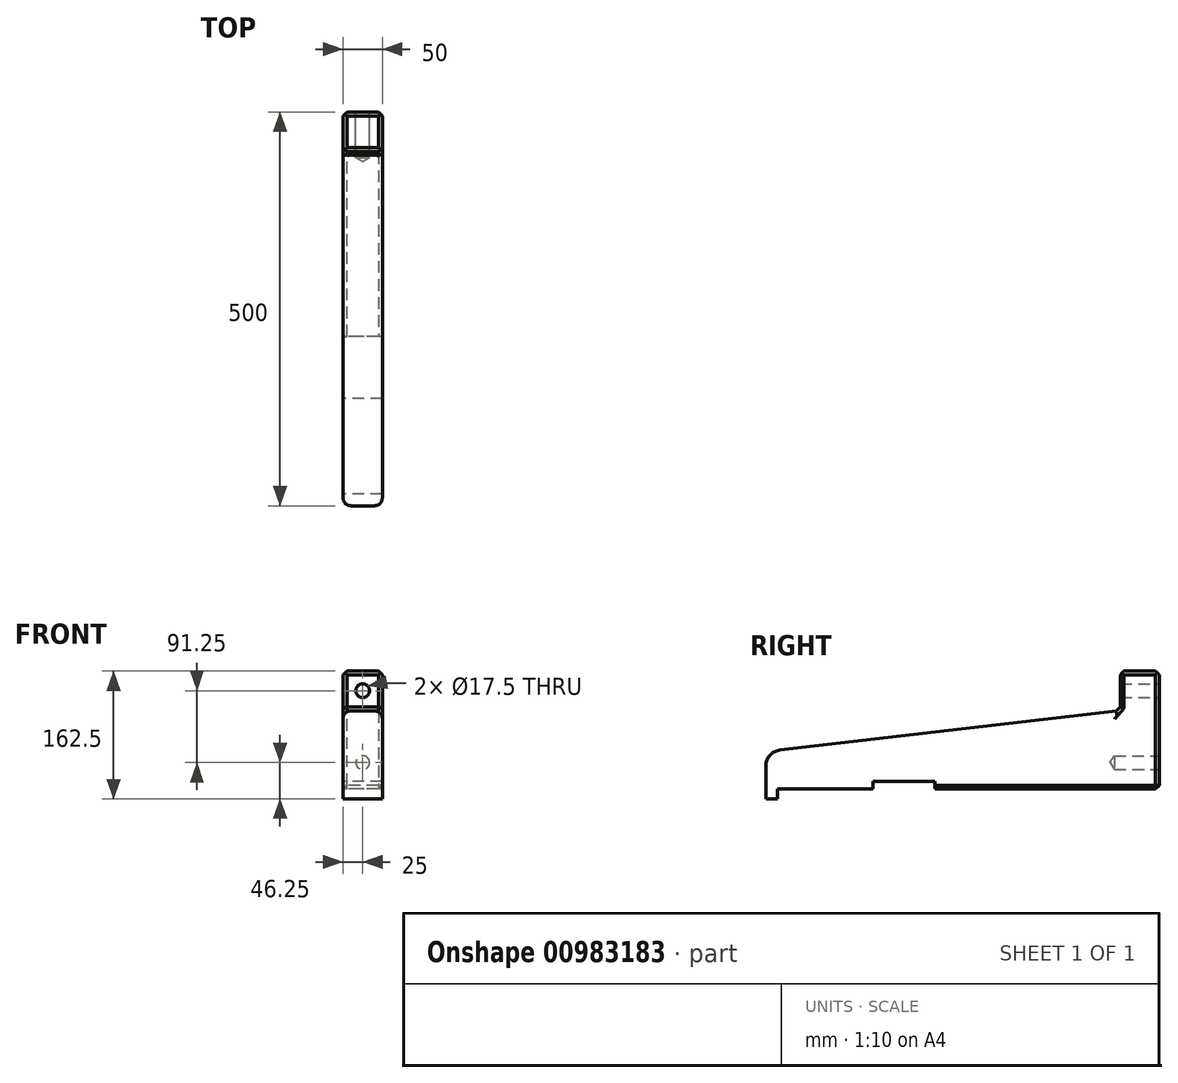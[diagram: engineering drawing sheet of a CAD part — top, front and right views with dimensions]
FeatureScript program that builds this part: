
annotation { "Feature Type Name" : "Feature", "Feature Type Description" : "" }
export const myFeature = defineFeature(function(context is Context, id is Id, definition is map)
    precondition{}
    {
        {
            var Q0;
            Q0=qCreatedBy(makeId("Right.planeOp"),FACE);
            var sketch = newSketch(context, id + "F0", { "sketchPlane" : qUnion([Q0])});
            skLineSegment(sketch, "E0", {"start": v(314, 100) * mm, "end": v(314, 150) * mm});
            skLineSegment(sketch, "E1", {"start": v(314, 150) * mm, "end": v(364, 150) * mm});
            skLineSegment(sketch, "E2", {"start": v(364, 150) * mm, "end": v(364, 0) * mm});
            skLineSegment(sketch, "E3", {"start": v(364, 0) * mm, "end": v(79, 0) * mm});
            skLineSegment(sketch, "E4", {"start": v(79, 0) * mm, "end": v(79, 10) * mm});
            skLineSegment(sketch, "E5", {"start": v(79, 10) * mm, "end": v(0, 10) * mm});
            skLineSegment(sketch, "E6", {"start": v(0, 10) * mm, "end": v(0, 0) * mm});
            skLineSegment(sketch, "E7", {"start": v(0, 0) * mm, "end": v(-121, 0) * mm});
            skLineSegment(sketch, "E8", {"start": v(-121, 0) * mm, "end": v(-121, -12.5) * mm});
            skLineSegment(sketch, "E9", {"start": v(-121, -12.5) * mm, "end": v(-136, -12.5) * mm});
            skLineSegment(sketch, "E10", {"start": v(-136, -12.5) * mm, "end": v(-136, 47.5) * mm});
            skLineSegment(sketch, "E11", {"start": v(314, 100) * mm, "end": v(-136, 47.5) * mm});
            skPoint(sketch, "E12.orphan", {"position": v(314, 50) * mm});
            skSolve(sketch);
        }
        {
            var Q0;
            Q0=makeQuery(id+"F0.imprint","IMPRINT",FACE,{"disambiguationData":[TD([[makeQuery(id+"F0.imprint","IMPRINT",EDGE,{"derivedFrom":sQuery(id+"F0.wireOp",EDGE,"E0")}),-1.0]])]});
            extrude(context, id + "F1", {"entities" : qUnion([Q0]), "depth" : 50 * mm, "offsetDistance" : 25 * mm});
        }
        {
            var Q0;
            Q0=makeQuery(id+"F1.opExtrude","SWEPT_FACE",FACE,{"disambiguationData":[OSD([sQuery(id+"F0.wireOp",EDGE,"E2")])]});
            var sketch = newSketch(context, id + "F2", { "sketchPlane" : qUnion([Q0])});
            skPoint(sketch, "E13", {"position": v(-25, 125) * mm});
            skPoint(sketch, "E14", {"position": v(-25, 25) * mm});
            skSolve(sketch);
        }
        {
            var Q0;
            Q0=sQuery(id+"F2.wireOp",VERTEX,"E13");
            var Q1;
            Q1=makeQuery(id+"F1.opExtrude","SWEPT_BODY",BODY,{"disambiguationData":[OSD([sQuery(id+"F0.wireOp",EDGE,"E0"),sQuery(id+"F0.wireOp",EDGE,"E1"),sQuery(id+"F0.wireOp",EDGE,"E2"),sQuery(id+"F0.wireOp",EDGE,"E3"),sQuery(id+"F0.wireOp",EDGE,"E4"),sQuery(id+"F0.wireOp",EDGE,"E5"),sQuery(id+"F0.wireOp",EDGE,"E6"),sQuery(id+"F0.wireOp",EDGE,"E7"),sQuery(id+"F0.wireOp",EDGE,"E8"),sQuery(id+"F0.wireOp",EDGE,"E9"),sQuery(id+"F0.wireOp",EDGE,"E10"),sQuery(id+"F0.wireOp",EDGE,"E11")])]});
            hole(context, id + "F3", {"style" : HoleStyle.SIMPLE, "endStyle" : HoleEndStyle.THROUGH, "standardTappedOrClearance" : lookupTablePath({ "standard" : "ISO", "fit" : "Normal", "engagement" : "75%", "pitch" : "2.5 mm", "size" : "M20", "type" : "Tapped" }), "standardBlindInLast" : lookupTablePath({ "fit" : "Normal", "standard" : "ISO", "engagement" : "75%", "pitch" : "2.5 mm", "size" : "M20", "type" : "Clearance & tapped" }), "holeDiameter" : 17.5 * mm, "majorDiameter" : 20 * mm, "showTappedDepth" : true, "isTappedThrough" : true, "tappedDepth" : 12 * mm, "tapClearance" : 3, "locations" : qUnion([Q0]), "scope" : qUnion([Q1])});
        }
        {
            var Q0;
            Q0=makeQuery(id+"F1.opExtrude","SWEPT_EDGE",EDGE,{"disambiguationData":[OSD([sQuery(id+"F0.wireOp",EDGE,"E10"),sQuery(id+"F0.wireOp",EDGE,"E11")])]});
            fillet(context, id + "F4", {"entities" : qUnion([Q0]), "tangentPropagation" : true, "radius" : 20 * mm, "defaultsChanged" : true, "vertexSettings" : [], "allowEdgeOverflow" : false});
        }
        {
            var Q0;
            Q0=makeQuery(id+"F1.opExtrude","SWEPT_EDGE",EDGE,{"disambiguationData":[OSD([sQuery(id+"F0.wireOp",EDGE,"E0"),sQuery(id+"F0.wireOp",EDGE,"E1")])]});
            var Q1;
            Q1=makeQuery(id+"F1.opExtrude","SWEPT_FACE",FACE,{"disambiguationData":[OSD([sQuery(id+"F0.wireOp",EDGE,"E1")])]});
            chamfer(context, id + "F5", {"entities" : qUnion([Q0, Q1]), "width" : 5 * mm, "tangentPropagation" : true});
        }
        {
            var Q0;
            Q0=makeQuery(id+"F1.opExtrude","CAP_EDGE",EDGE,{"disambiguationData":[OSD([sQuery(id+"F0.wireOp",EDGE,"E2")])],"isStart":false});
            var Q1;
            Q1=makeQuery(id+"F1.opExtrude","CAP_EDGE",EDGE,{"disambiguationData":[OSD([sQuery(id+"F0.wireOp",EDGE,"E2")])],"isStart":true});
            var Q2;
            Q2=makeQuery(id+"F1.opExtrude","SWEPT_EDGE",EDGE,{"disambiguationData":[OSD([sQuery(id+"F0.wireOp",EDGE,"E2"),sQuery(id+"F0.wireOp",EDGE,"E3")])]});
            var Q3;
            Q3=makeQuery(id+"F1.opExtrude","CAP_EDGE",EDGE,{"disambiguationData":[OSD([sQuery(id+"F0.wireOp",EDGE,"E3")])],"isStart":true});
            var Q4;
            Q4=makeQuery(id+"F1.opExtrude","CAP_EDGE",EDGE,{"disambiguationData":[OSD([sQuery(id+"F0.wireOp",EDGE,"E3")])],"isStart":false});
            var Q5;
            Q5=makeQuery(id+"F1.opExtrude","SWEPT_EDGE",EDGE,{"disambiguationData":[OSD([sQuery(id+"F0.wireOp",EDGE,"E0"),sQuery(id+"F0.wireOp",EDGE,"E11")])]});
            chamfer(context, id + "F6", {"entities" : qUnion([Q0, Q1, Q2, Q3, Q4, Q5]), "width" : 5 * mm, "tangentPropagation" : true});
        }
        {
            var Q0;
            Q0=makeQuery(id+"F1.opExtrude","CAP_EDGE",EDGE,{"disambiguationData":[OSD([sQuery(id+"F0.wireOp",EDGE,"E11")])],"isStart":true});
            var Q1;
            Q1=makeQuery(id+"F1.opExtrude","CAP_EDGE",EDGE,{"disambiguationData":[OSD([sQuery(id+"F0.wireOp",EDGE,"E11")])],"isStart":false});
            fillet(context, id + "F7", {"entities" : qUnion([Q0, Q1]), "tangentPropagation" : true, "radius" : 10 * mm, "defaultsChanged" : true, "vertexSettings" : [], "allowEdgeOverflow" : false});
        }
        {
            var Q0;
            Q0=makeQuery(id+"F1.opExtrude","CAP_EDGE",EDGE,{"disambiguationData":[OSD([sQuery(id+"F0.wireOp",EDGE,"E0")])],"isStart":true});
            var Q1;
            Q1=makeQuery(id+"F1.opExtrude","CAP_EDGE",EDGE,{"disambiguationData":[OSD([sQuery(id+"F0.wireOp",EDGE,"E0")])],"isStart":false});
            var Q2;
            {var subQ0=sQuery(id+"F0.wireOp",EDGE,"E11");var subQ1=sQuery(id+"F0.wireOp",EDGE,"E0");Q2=makeQuery(id+"F6.opChamfer","BLEND_EDGE",EDGE,{"blendedFrom":[makeQuery(id+"F1.opExtrude","SWEPT_EDGE",EDGE,{"disambiguationData":[OSD([subQ1,subQ0])]}),makeQuery(id+"F1.opExtrude","CAP_FACE",FACE,{"disambiguationData":[OSD([subQ1,sQuery(id+"F0.wireOp",EDGE,"E1"),sQuery(id+"F0.wireOp",EDGE,"E2"),sQuery(id+"F0.wireOp",EDGE,"E3"),sQuery(id+"F0.wireOp",EDGE,"E4"),sQuery(id+"F0.wireOp",EDGE,"E5"),sQuery(id+"F0.wireOp",EDGE,"E6"),sQuery(id+"F0.wireOp",EDGE,"E7"),sQuery(id+"F0.wireOp",EDGE,"E8"),sQuery(id+"F0.wireOp",EDGE,"E9"),sQuery(id+"F0.wireOp",EDGE,"E10"),subQ0])],"isStart":true})],"blendedInto":[makeQuery(id+"F1.opExtrude","CAP_FACE",FACE,{"disambiguationData":[OSD([subQ1,sQuery(id+"F0.wireOp",EDGE,"E1"),sQuery(id+"F0.wireOp",EDGE,"E2"),sQuery(id+"F0.wireOp",EDGE,"E3"),sQuery(id+"F0.wireOp",EDGE,"E4"),sQuery(id+"F0.wireOp",EDGE,"E5"),sQuery(id+"F0.wireOp",EDGE,"E6"),sQuery(id+"F0.wireOp",EDGE,"E7"),sQuery(id+"F0.wireOp",EDGE,"E8"),sQuery(id+"F0.wireOp",EDGE,"E9"),sQuery(id+"F0.wireOp",EDGE,"E10"),subQ0])],"isStart":true})]});}
            var Q3;
            {var subQ0=sQuery(id+"F0.wireOp",EDGE,"E11");var subQ1=sQuery(id+"F0.wireOp",EDGE,"E0");Q3=makeQuery(id+"F6.opChamfer","BLEND_EDGE",EDGE,{"blendedFrom":[makeQuery(id+"F1.opExtrude","SWEPT_EDGE",EDGE,{"disambiguationData":[OSD([subQ1,subQ0])]}),makeQuery(id+"F1.opExtrude","CAP_FACE",FACE,{"disambiguationData":[OSD([subQ1,sQuery(id+"F0.wireOp",EDGE,"E1"),sQuery(id+"F0.wireOp",EDGE,"E2"),sQuery(id+"F0.wireOp",EDGE,"E3"),sQuery(id+"F0.wireOp",EDGE,"E4"),sQuery(id+"F0.wireOp",EDGE,"E5"),sQuery(id+"F0.wireOp",EDGE,"E6"),sQuery(id+"F0.wireOp",EDGE,"E7"),sQuery(id+"F0.wireOp",EDGE,"E8"),sQuery(id+"F0.wireOp",EDGE,"E9"),sQuery(id+"F0.wireOp",EDGE,"E10"),subQ0])],"isStart":false})],"blendedInto":[makeQuery(id+"F1.opExtrude","CAP_FACE",FACE,{"disambiguationData":[OSD([subQ1,sQuery(id+"F0.wireOp",EDGE,"E1"),sQuery(id+"F0.wireOp",EDGE,"E2"),sQuery(id+"F0.wireOp",EDGE,"E3"),sQuery(id+"F0.wireOp",EDGE,"E4"),sQuery(id+"F0.wireOp",EDGE,"E5"),sQuery(id+"F0.wireOp",EDGE,"E6"),sQuery(id+"F0.wireOp",EDGE,"E7"),sQuery(id+"F0.wireOp",EDGE,"E8"),sQuery(id+"F0.wireOp",EDGE,"E9"),sQuery(id+"F0.wireOp",EDGE,"E10"),subQ0])],"isStart":false})]});}
            chamfer(context, id + "F8", {"entities" : qUnion([Q0, Q1, Q2, Q3]), "width" : 5 * mm, "tangentPropagation" : true});
        }
        {
            var Q0;
            Q0=makeQuery(id+"F1.opExtrude","SWEPT_FACE",FACE,{"disambiguationData":[OSD([sQuery(id+"F0.wireOp",EDGE,"E2")])]});
            var sketch = newSketch(context, id + "F9", { "sketchPlane" : qUnion([Q0])});
            skPoint(sketch, "E15", {"position": v(-25, 33.75) * mm});
            skSolve(sketch);
        }
        {
            var Q0;
            Q0=sQuery(id+"F9.wireOp",VERTEX,"E15");
            var Q1;
            Q1=makeQuery(id+"F1.opExtrude","SWEPT_BODY",BODY,{"disambiguationData":[OSD([sQuery(id+"F0.wireOp",EDGE,"E0"),sQuery(id+"F0.wireOp",EDGE,"E1"),sQuery(id+"F0.wireOp",EDGE,"E2"),sQuery(id+"F0.wireOp",EDGE,"E3"),sQuery(id+"F0.wireOp",EDGE,"E4"),sQuery(id+"F0.wireOp",EDGE,"E5"),sQuery(id+"F0.wireOp",EDGE,"E6"),sQuery(id+"F0.wireOp",EDGE,"E7"),sQuery(id+"F0.wireOp",EDGE,"E8"),sQuery(id+"F0.wireOp",EDGE,"E9"),sQuery(id+"F0.wireOp",EDGE,"E10"),sQuery(id+"F0.wireOp",EDGE,"E11")])]});
            hole(context, id + "F10", {"style" : HoleStyle.SIMPLE, "endStyle" : HoleEndStyle.BLIND, "standardTappedOrClearance" : lookupTablePath({ "standard" : "ISO", "fit" : "Normal", "engagement" : "75%", "pitch" : "2.5 mm", "size" : "M20", "type" : "Tapped" }), "standardBlindInLast" : lookupTablePath({ "fit" : "Normal", "standard" : "ISO", "engagement" : "75%", "pitch" : "2.5 mm", "size" : "M20", "type" : "Clearance & tapped" }), "holeDiameter" : 17.5 * mm, "majorDiameter" : 20 * mm, "showTappedDepth" : true, "holeDepth" : 57.5 * mm, "tappedDepth" : 50 * mm, "tapClearance" : 3, "startFromSketch" : true, "locations" : qUnion([Q0]), "scope" : qUnion([Q1])});
        }
    });
